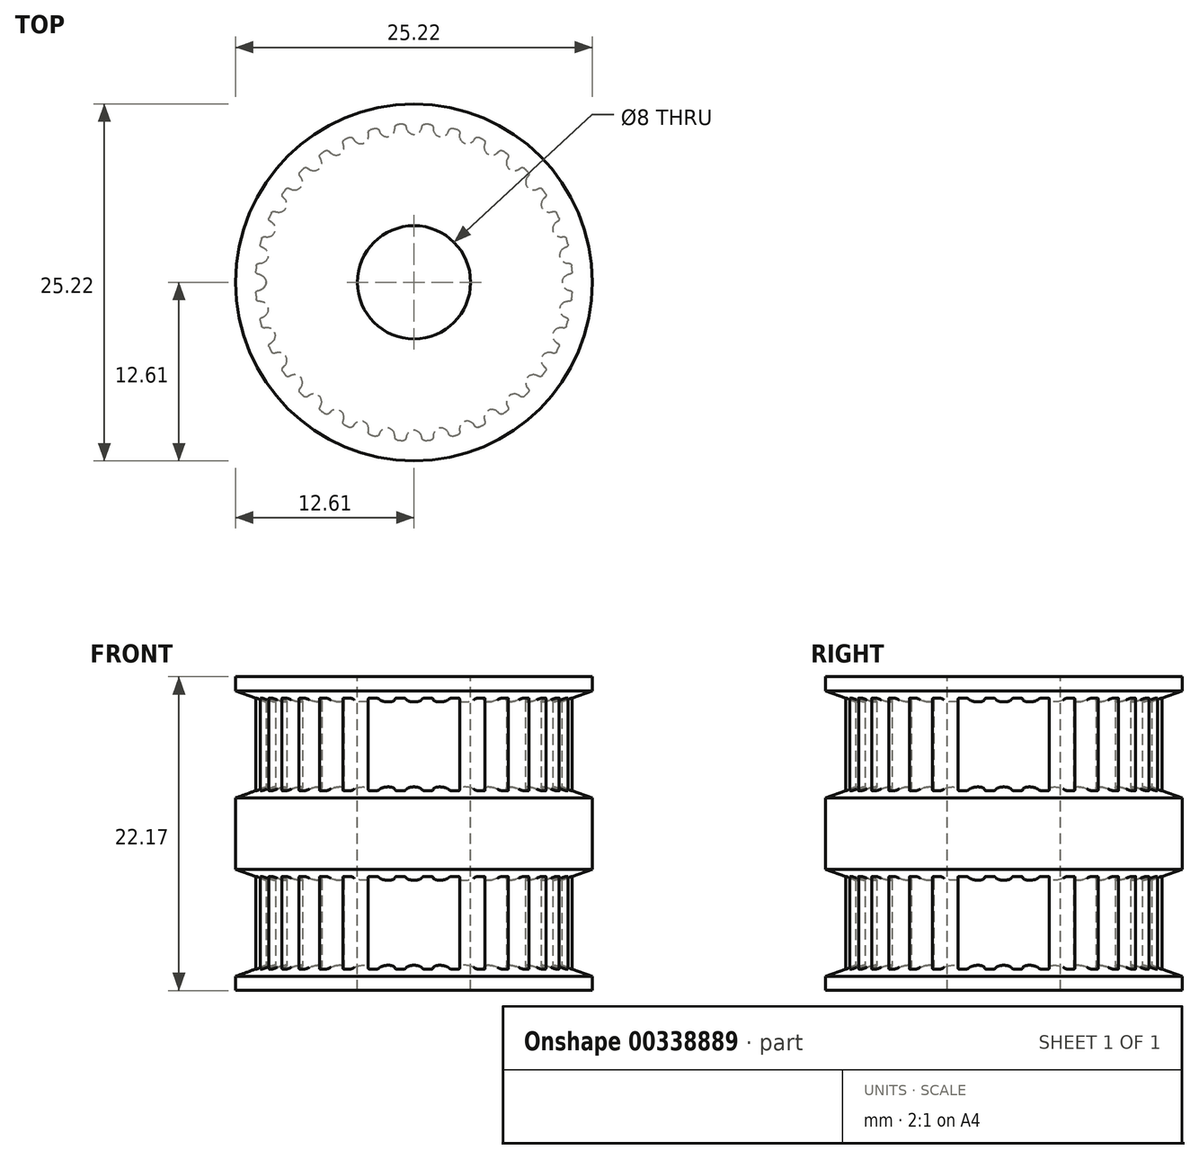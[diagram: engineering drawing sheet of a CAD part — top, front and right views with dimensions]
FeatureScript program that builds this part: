
annotation { "Feature Type Name" : "Feature", "Feature Type Description" : "" }
export const myFeature = defineFeature(function(context is Context, id is Id, definition is map)
    precondition{}
    {
        {
            assignVariable(context, id + "F0", {"name" : "teeth", "anyValue" : 36});
        }
        {
            assignVariable(context, id + "F1", {"name" : "total_length", "anyValue" : 22});
        }
        {
            var Q0;
            Q0=qCreatedBy(makeId("Top.planeOp"),FACE);
            var sketch = newSketch(context, id + "F2", { "sketchPlane" : qUnion([Q0])});
            skLineSegment(sketch, "E0", {"start": v(0, 0) * mm, "end": v(0, 10.46) * mm, "construction": true});
            skCircle(sketch, "E1", {"center": v(0, 0) * mm, "radius": 11.2 * mm});
            skPoint(sketch, "E2.MirrorCS.end.orphan", {"position": v(0.98, 11.16) * mm});
            skLineSegment(sketch, "E3", {"start": v(0.98, 11.16) * mm, "end": v(1, 11.42) * mm, "construction": true});
            skLineSegment(sketch, "E4", {"start": v(-0.98, 11.16) * mm, "end": v(-1, 11.42) * mm, "construction": true});
            skArc(sketch, "E5", {"start": v(0, 10.46) * mm, "mid": v(0.34, 10.57) * mm, "end": v(0.53, 10.86) * mm});
            skArc(sketch, "E6", {"start": v(0.53, 10.86) * mm, "mid": v(0.56, 10.96) * mm, "end": v(0.58, 11.05) * mm, "construction": true});
            skLineSegment(sketch, "E7", {"start": v(0, 10.46) * mm, "end": v(0, 11.2) * mm, "construction": true});
            skLineSegment(sketch, "E8", {"start": v(0, 11.2) * mm, "end": v(0, 11.46) * mm, "construction": true});
            skArc(sketch, "E9", {"start": v(0.58, 11.05) * mm, "mid": v(0.64, 11.15) * mm, "end": v(0.74, 11.18) * mm, "construction": true});
            skArc(sketch, "E10", {"start": v(1, 11.42) * mm, "mid": v(0, 11.46) * mm, "end": v(-1, 11.42) * mm, "construction": true});
            skLineSegment(sketch, "E11", {"start": v(0.98, 11.16) * mm, "end": v(0.91, 10.42) * mm});
            skLineSegment(sketch, "E12", {"start": v(0.91, 10.42) * mm, "end": v(0, 0) * mm});
            skLineSegment(sketch, "E13", {"start": v(0, 0) * mm, "end": v(-0.91, 10.42) * mm});
            skLineSegment(sketch, "E14", {"start": v(-0.91, 10.42) * mm, "end": v(-0.98, 11.16) * mm});
            skArc(sketch, "E15", {"start": v(0.78, 11.18) * mm, "mid": v(0.65, 11.14) * mm, "end": v(0.58, 11.04) * mm});
            skArc(sketch, "E16", {"start": v(0.53, 10.86) * mm, "mid": v(0.56, 10.95) * mm, "end": v(0.58, 11.04) * mm});
            skArc(sketch, "E17.MirrorCS", {"start": v(0, 10.46) * mm, "mid": v(-0.34, 10.57) * mm, "end": v(-0.53, 10.86) * mm});
            skArc(sketch, "E18.MirrorCS", {"start": v(-0.53, 10.86) * mm, "mid": v(-0.56, 10.95) * mm, "end": v(-0.58, 11.04) * mm});
            skArc(sketch, "E19.MirrorCS", {"start": v(-0.78, 11.18) * mm, "mid": v(-0.65, 11.14) * mm, "end": v(-0.58, 11.04) * mm});
            skArc(sketch, "E20", {"start": v(0, 11.2) * mm, "mid": v(-0.2, 11.2) * mm, "end": v(-0.4, 11.2) * mm});
            skArc(sketch, "E21", {"start": v(0.91, 10.42) * mm, "mid": v(0, 10.46) * mm, "end": v(-0.91, 10.42) * mm, "construction": true});
            skLineSegment(sketch, "E22", {"start": v(1, 11.42) * mm, "end": v(1.03, 11.8) * mm, "construction": true});
            skLineSegment(sketch, "E23", {"start": v(-1, 11.42) * mm, "end": v(-1.03, 11.8) * mm, "construction": true});
            skArc(sketch, "E24", {"start": v(-1.03, 11.8) * mm, "mid": v(0, 11.84) * mm, "end": v(1.03, 11.8) * mm, "construction": true});
            skSolve(sketch);
        }
        {
            var Q0;
            Q0=makeQuery(id+"F2.imprint","IMPRINT",FACE,{"disambiguationData":[TD([[makeQuery(id+"F2.imprint","IMPRINT",EDGE,{"derivedFrom":sQuery(id+"F2.wireOp",EDGE,"E5")}),-1.0]])]});
            var Q1;
            {var subQ1=sQuery(id+"F2.wireOp",EDGE,"E14");Q1=makeQuery(id+"F2.imprint","IMPRINT",FACE,{"disambiguationData":[TD([[makeQuery(id+"F2.imprint","IMPRINT",EDGE,{"derivedFrom":subQ1}),-1.0]])]});}
            var Q2;
            {var subQ0=sQuery(id+"F2.wireOp",EDGE,"E12");Q2=makeQuery(id+"F2.imprint","IMPRINT",FACE,{"disambiguationData":[TD([[makeQuery(id+"F2.imprint","IMPRINT",EDGE,{"derivedFrom":subQ0}),-1.0]])]});}
            extrude(context, id + "F3", {"entities" : qUnion([Q0, Q1, Q2]), "endBound" : BoundingType.SYMMETRIC, "depth" : (getVariable(context, 'total_length')) * mm});
        }
        {
            var Q0;
            Q0=makeQuery(id+"F3.opExtrude","SWEPT_BODY",BODY,{"disambiguationData":[OSD([sQuery(id+"F2.wireOp",EDGE,"E1"),sQuery(id+"F2.wireOp",EDGE,"E5"),sQuery(id+"F2.wireOp",EDGE,"E11"),sQuery(id+"F2.wireOp",EDGE,"E12"),sQuery(id+"F2.wireOp",EDGE,"E13"),sQuery(id+"F2.wireOp",EDGE,"E14"),sQuery(id+"F2.wireOp",EDGE,"E15"),sQuery(id+"F2.wireOp",EDGE,"E16"),sQuery(id+"F2.wireOp",EDGE,"E17.MirrorCS"),sQuery(id+"F2.wireOp",EDGE,"E18.MirrorCS"),sQuery(id+"F2.wireOp",EDGE,"E19.MirrorCS")])]});
            var Q1;
            Q1=makeQuery(id+"F3.opExtrude","SWEPT_EDGE",EDGE,{"disambiguationData":[OSD([sQuery(id+"F2.wireOp",EDGE,"E12"),sQuery(id+"F2.wireOp",EDGE,"E13")])]});
            circularPattern(context, id + "F4", {"operationType" : NewBodyOperationType.ADD, "entities" : qUnion([Q0]), "axis" : qUnion([Q1]), "angle" : 360 * degree, "instanceCount" : getVariable(context, 'teeth'), "equalSpace" : true});
        }
        {
            var Q0;
            Q0=qCreatedBy(makeId("Front.planeOp"),FACE);
            var sketch = newSketch(context, id + "F5", { "sketchPlane" : qUnion([Q0])});
            skLineSegment(sketch, "E25", {"start": v(0, 11) * mm, "end": v(12.6, 11) * mm});
            skLineSegment(sketch, "E26", {"start": v(12.6, 11) * mm, "end": v(12.6, 10) * mm});
            skLineSegment(sketch, "E27", {"start": v(12.6, 10) * mm, "end": v(10.46, 9.22) * mm});
            skLineSegment(sketch, "E28", {"start": v(10.46, 9.22) * mm, "end": v(0, 9.22) * mm});
            skLineSegment(sketch, "E29", {"start": v(0, 9.22) * mm, "end": v(0, 11) * mm});
            skLineSegment(sketch, "E30", {"start": v(0, 3.22) * mm, "end": v(10.46, 3.22) * mm});
            skLineSegment(sketch, "E31", {"start": v(10.46, 3.22) * mm, "end": v(12.6, 2.43) * mm});
            skLineSegment(sketch, "E32", {"start": v(12.6, 2.43) * mm, "end": v(12.6, -2.6) * mm});
            skLineSegment(sketch, "E33", {"start": v(12.6, -2.6) * mm, "end": v(10.46, -3.38) * mm});
            skLineSegment(sketch, "E34", {"start": v(10.46, -3.38) * mm, "end": v(0, -3.38) * mm});
            skLineSegment(sketch, "E35", {"start": v(0, -3.38) * mm, "end": v(0, 3.22) * mm});
            skLineSegment(sketch, "E36", {"start": v(0, -9.38) * mm, "end": v(10.46, -9.38) * mm});
            skLineSegment(sketch, "E37", {"start": v(10.46, -9.38) * mm, "end": v(12.6, -10.17) * mm});
            skLineSegment(sketch, "E38", {"start": v(12.6, -10.17) * mm, "end": v(12.6, -11.17) * mm});
            skLineSegment(sketch, "E39", {"start": v(12.6, -11.17) * mm, "end": v(0, -11.17) * mm});
            skLineSegment(sketch, "E40", {"start": v(0, -11.17) * mm, "end": v(0, -9.38) * mm});
            skSolve(sketch);
        }
        {
            var Q0;
            Q0 = qSketchRegion(id + "F5", true);
            var Q1;
            Q1=sQuery(id+"F5.wireOp",EDGE,"E35");
            revolve(context, id + "F6", {"operationType" : NewBodyOperationType.ADD, "entities" : qUnion([Q0]), "axis" : qUnion([Q1]), "revolveType" : RevolveType.FULL});
        }
        {
            var Q0;
            Q0=qCreatedBy(makeId("Top.planeOp"),FACE);
            var sketch = newSketch(context, id + "F7", { "sketchPlane" : qUnion([Q0])});
            skCircle(sketch, "E41", {"center": v(0, 0) * mm, "radius": 4 * mm});
            skSolve(sketch);
        }
        {
            var Q0;
            Q0 = qSketchRegion(id + "F7", true);
            extrude(context, id + "F8", {"entities" : qUnion([Q0]), "operationType" : NewBodyOperationType.REMOVE, "endBound" : BoundingType.SYMMETRIC, "oppositeDirection" : true, "depth" : 100 * mm});
        }
    });
